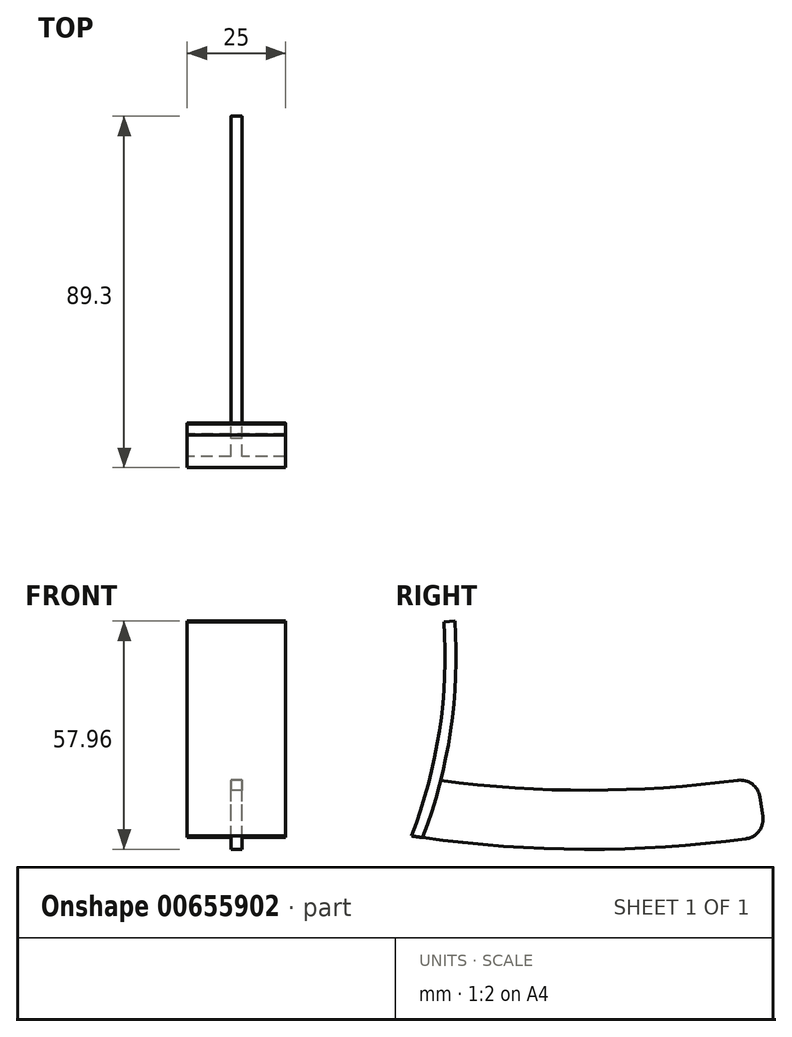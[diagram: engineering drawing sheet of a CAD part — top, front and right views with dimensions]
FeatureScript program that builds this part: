
annotation { "Feature Type Name" : "Feature", "Feature Type Description" : "" }
export const myFeature = defineFeature(function(context is Context, id is Id, definition is map)
    precondition{}
    {
        {
            var Q0;
            Q0=qCreatedBy(makeId("Right.planeOp"),FACE);
            var sketch = newSketch(context, id + "F0", { "sketchPlane" : qUnion([Q0])});
            skArc(sketch, "E0", {"start": v(-45, 3.4) * mm, "mid": v(0, 0) * mm, "end": v(45, 3.4) * mm});
            skLineSegment(sketch, "E1", {"start": v(-45, 3.4) * mm, "end": v(-36.75, 57.77) * mm, "construction": true});
            skArc(sketch, "E2", {"start": v(-45, 3.4) * mm, "mid": v(-37.9, 30.13) * mm, "end": v(-36.75, 57.77) * mm});
            skLineSegment(sketch, "E3", {"start": v(0, 0) * mm, "end": v(0, 300) * mm, "construction": true});
            skLineSegment(sketch, "E4", {"start": v(45, 3.4) * mm, "end": v(44.58, 6.16) * mm});
            skLineSegment(sketch, "E5", {"start": v(-36.75, 57.77) * mm, "end": v(-33.96, 57.96) * mm});
            skArc(sketch, "E6", {"start": v(-41.17, 5.67) * mm, "mid": v(-34.9, 31.44) * mm, "end": v(-33.96, 57.96) * mm});
            skArc(sketch, "E7", {"start": v(-41.17, 5.67) * mm, "mid": v(1.72, 2.8) * mm, "end": v(44.58, 6.16) * mm});
            skSolve(sketch);
        }
        {
            var Q0;
            Q0 = qSketchRegion(id + "F0", true);
            extrude(context, id + "F1", {"entities" : qUnion([Q0]), "depth" : 2.8 * mm, "offsetDistance" : 25 * mm, "symmetric" : true});
        }
        {
            var Q0;
            Q0=qCreatedBy(makeId("Right.planeOp"),FACE);
            var sketch = newSketch(context, id + "F2", { "sketchPlane" : qUnion([Q0])});
            skLineSegment(sketch, "E8.0", {"start": v(-36.75, 57.77) * mm, "end": v(-33.96, 57.96) * mm});
            skArc(sketch, "E9.0", {"start": v(-45, 3.4) * mm, "mid": v(-37.9, 30.13) * mm, "end": v(-36.75, 57.77) * mm});
            skArc(sketch, "E10.0", {"start": v(-42.16, 2.98) * mm, "mid": v(-35.1, 30.03) * mm, "end": v(-33.96, 57.96) * mm});
            skArc(sketch, "E11.0", {"start": v(-45, 3.4) * mm, "mid": v(-43.58, 3.18) * mm, "end": v(-42.16, 2.98) * mm});
            skPoint(sketch, "E12.orphan", {"position": v(-41.17, 5.67) * mm});
            skPoint(sketch, "E13.orphan", {"position": v(45, 3.4) * mm});
            skSolve(sketch);
        }
        {
            var Q0;
            Q0 = qSketchRegion(id + "F2", true);
            extrude(context, id + "F3", {"entities" : qUnion([Q0]), "operationType" : NewBodyOperationType.ADD, "depth" : 25 * mm, "offsetDistance" : 25 * mm, "symmetric" : true});
        }
        {
            var Q0;
            Q0=qCreatedBy(makeId("Right.planeOp"),FACE);
            var sketch = newSketch(context, id + "F4", { "sketchPlane" : qUnion([Q0])});
            skLineSegment(sketch, "E14", {"start": v(44.58, 6.16) * mm, "end": v(42.75, 18.22) * mm});
            skArc(sketch, "E15", {"start": v(-41.17, 5.67) * mm, "mid": v(1.72, 2.8) * mm, "end": v(44.58, 6.16) * mm});
            skArc(sketch, "E16", {"start": v(-41.17, 5.67) * mm, "mid": v(-39.25, 11.54) * mm, "end": v(-37.6, 17.5) * mm});
            skArc(sketch, "E17", {"start": v(-37.6, 17.5) * mm, "mid": v(2.6, 15.01) * mm, "end": v(42.75, 18.22) * mm});
            skSolve(sketch);
        }
        {
            var Q0;
            Q0 = qSketchRegion(id + "F4", true);
            extrude(context, id + "F5", {"entities" : qUnion([Q0]), "operationType" : NewBodyOperationType.ADD, "depth" : 2.8 * mm, "offsetDistance" : 25 * mm, "symmetric" : true});
        }
        {
            var Q0;
            Q0=makeQuery(id+"F5.opExtrude","SWEPT_EDGE",EDGE,{"disambiguationData":[OSD([sQuery(id+"F4.wireOp",EDGE,"E14"),sQuery(id+"F4.wireOp",EDGE,"E17")])]});
            var Q1;
            Q1=makeQuery(id+"F1.opExtrude","SWEPT_EDGE",EDGE,{"disambiguationData":[OSD([sQuery(id+"F0.wireOp",EDGE,"E0"),sQuery(id+"F0.wireOp",EDGE,"E4")])]});
            fillet(context, id + "F6", {"entities" : qUnion([Q0, Q1]), "radius" : 5 * mm, "tangentPropagation" : true, "allowEdgeOverflow" : false});
        }
    });
